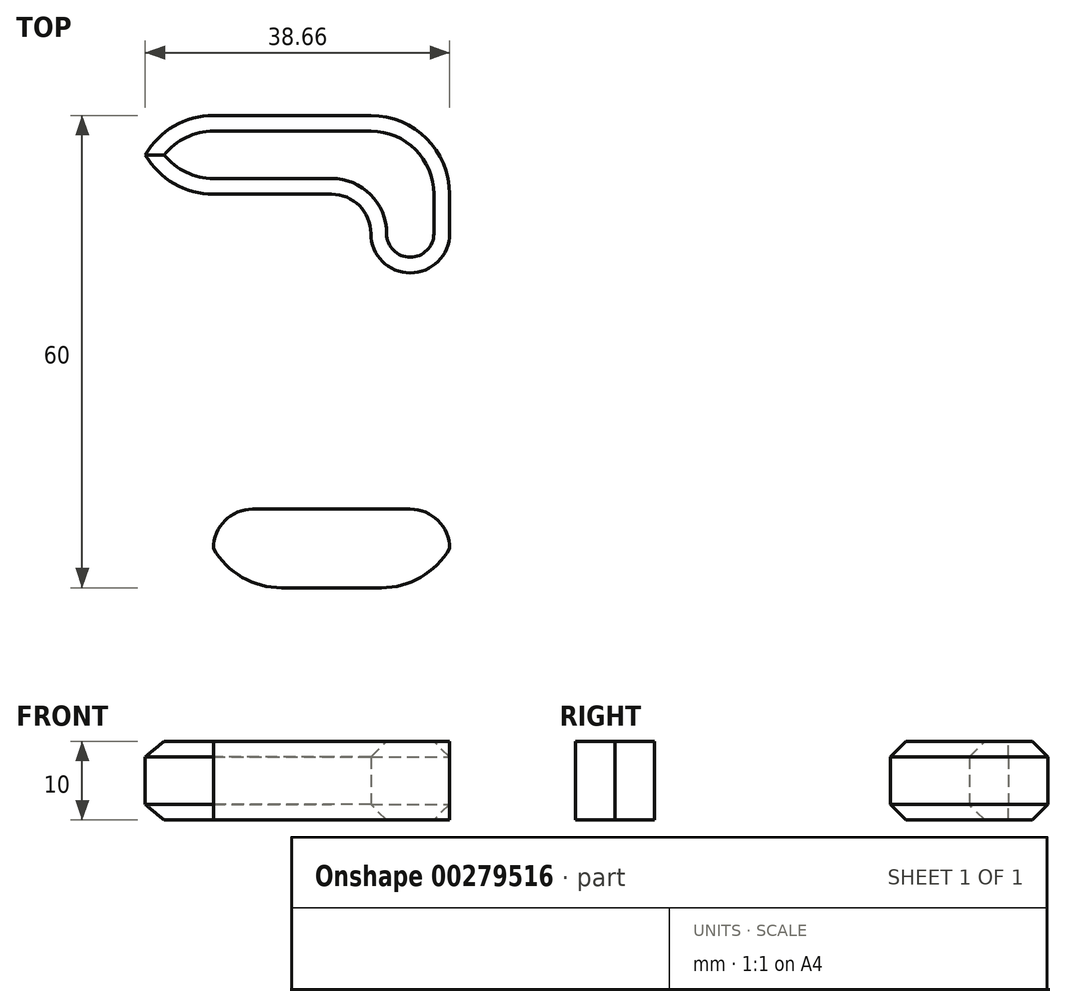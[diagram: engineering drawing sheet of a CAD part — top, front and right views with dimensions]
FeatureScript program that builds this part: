
annotation { "Feature Type Name" : "Feature", "Feature Type Description" : "" }
export const myFeature = defineFeature(function(context is Context, id is Id, definition is map)
    precondition{}
    {
        {
            var Q0;
            Q0=qCreatedBy(makeId("Top.planeOp"),FACE);
            var sketch = newSketch(context, id + "F0", { "sketchPlane" : qUnion([Q0])});
            skLineSegment(sketch, "E0.bottom", {"start": v(6.47, 40) * mm, "end": v(16.47, 40) * mm});
            skLineSegment(sketch, "E0.top", {"start": v(6.47, 20) * mm, "end": v(16.47, 20) * mm});
            skLineSegment(sketch, "E0.left", {"start": v(6.47, 40) * mm, "end": v(6.47, 20) * mm});
            skLineSegment(sketch, "E0.right", {"start": v(16.47, 40) * mm, "end": v(16.47, 20) * mm});
            skLineSegment(sketch, "E1.bottom", {"start": v(6.47, 40) * mm, "end": v(-23.53, 40) * mm});
            skLineSegment(sketch, "E1.top", {"start": v(6.47, 30) * mm, "end": v(-23.53, 30) * mm});
            skLineSegment(sketch, "E1.left", {"start": v(6.47, 40) * mm, "end": v(6.47, 30) * mm});
            skLineSegment(sketch, "E1.right", {"start": v(-23.53, 40) * mm, "end": v(-23.53, 30) * mm});
            skLineSegment(sketch, "E2.bottom", {"start": v(-23.53, 30) * mm, "end": v(-13.53, 30) * mm});
            skLineSegment(sketch, "E2.top", {"start": v(-23.53, -20) * mm, "end": v(-13.53, -20) * mm});
            skLineSegment(sketch, "E2.left", {"start": v(-23.53, 30) * mm, "end": v(-23.53, -20) * mm});
            skLineSegment(sketch, "E2.right", {"start": v(-13.53, 30) * mm, "end": v(-13.53, -20) * mm});
            skPoint(sketch, "E3.oppositeSnap0", {"position": v(-18.53, -20) * mm});
            skLineSegment(sketch, "E3.bottom", {"start": v(-13.53, -10) * mm, "end": v(16.47, -10) * mm});
            skLineSegment(sketch, "E3.top", {"start": v(-13.53, -20) * mm, "end": v(16.47, -20) * mm});
            skLineSegment(sketch, "E3.left", {"start": v(-13.53, -10) * mm, "end": v(-13.53, -20) * mm});
            skLineSegment(sketch, "E3.right", {"start": v(16.47, -10) * mm, "end": v(16.47, -20) * mm});
            skLineSegment(sketch, "E4.bottom", {"start": v(16.47, -10) * mm, "end": v(6.47, -10) * mm});
            skLineSegment(sketch, "E4.top", {"start": v(16.47, 0) * mm, "end": v(6.47, 0) * mm});
            skLineSegment(sketch, "E4.left", {"start": v(16.47, -10) * mm, "end": v(16.47, 0) * mm});
            skLineSegment(sketch, "E4.right", {"start": v(6.47, -10) * mm, "end": v(6.47, 0) * mm});
            skSolve(sketch);
        }
        {
            var Q0;
            Q0=makeQuery(id+"F0.imprint","IMPRINT",FACE,{"disambiguationData":[TD([[makeQuery(id+"F0.imprint","IMPRINT",EDGE,{"derivedFrom":sQuery(id+"F0.wireOp",EDGE,"E1.bottom")}),1.0]])]});
            var Q1;
            Q1=makeQuery(id+"F0.imprint","IMPRINT",FACE,{"disambiguationData":[TD([[makeQuery(id+"F0.imprint","IMPRINT",EDGE,{"derivedFrom":sQuery(id+"F0.wireOp",EDGE,"E0.bottom")}),-1.0]])]});
            var Q2;
            Q2=makeQuery(id+"F0.imprint","IMPRINT",FACE,{"disambiguationData":[TD([[makeQuery(id+"F0.imprint","IMPRINT",EDGE,{"derivedFrom":sQuery(id+"F0.wireOp",EDGE,"E2.bottom")}),-1.0]])]});
            var Q3;
            Q3=makeQuery(id+"F0.imprint","IMPRINT",FACE,{"disambiguationData":[TD([[makeQuery(id+"F0.imprint","IMPRINT",EDGE,{"derivedFrom":sQuery(id+"F0.wireOp",EDGE,"E3.bottom")}),-1.0]])]});
            var Q4;
            Q4=makeQuery(id+"F0.imprint","IMPRINT",FACE,{"disambiguationData":[TD([[makeQuery(id+"F0.imprint","IMPRINT",EDGE,{"derivedFrom":sQuery(id+"F0.wireOp",EDGE,"E4.bottom")}),-1.0]])]});
            extrude(context, id + "F1", {"entities" : qUnion([Q0, Q1, Q2, Q3, Q4]), "depth" : 10 * mm});
        }
        {
            var Q0;
            Q0=makeQuery(id+"F1.opExtrude","SWEPT_EDGE",EDGE,{"disambiguationData":[OSD([sQuery(id+"F0.wireOp",EDGE,"E4.top"),sQuery(id+"F0.wireOp",EDGE,"E4.left")])]});
            var Q1;
            Q1=makeQuery(id+"F1.opExtrude","SWEPT_EDGE",EDGE,{"disambiguationData":[OSD([sQuery(id+"F0.wireOp",EDGE,"E4.top"),sQuery(id+"F0.wireOp",EDGE,"E4.right")])]});
            var Q2;
            Q2=makeQuery(id+"F1.opExtrude","SWEPT_EDGE",EDGE,{"disambiguationData":[OSD([sQuery(id+"F0.wireOp",EDGE,"E2.right"),sQuery(id+"F0.wireOp",EDGE,"E3.bottom"),sQuery(id+"F0.wireOp",EDGE,"E3.left")])]});
            var Q3;
            Q3=makeQuery(id+"F1.opExtrude","SWEPT_EDGE",EDGE,{"disambiguationData":[OSD([sQuery(id+"F0.wireOp",EDGE,"E3.bottom"),sQuery(id+"F0.wireOp",EDGE,"E4.bottom"),sQuery(id+"F0.wireOp",EDGE,"E4.right")])]});
            var Q4;
            Q4=makeQuery(id+"F1.opExtrude","SWEPT_EDGE",EDGE,{"disambiguationData":[OSD([sQuery(id+"F0.wireOp",EDGE,"E0.top"),sQuery(id+"F0.wireOp",EDGE,"E0.left")])]});
            var Q5;
            Q5=makeQuery(id+"F1.opExtrude","SWEPT_EDGE",EDGE,{"disambiguationData":[OSD([sQuery(id+"F0.wireOp",EDGE,"E0.left"),sQuery(id+"F0.wireOp",EDGE,"E1.top"),sQuery(id+"F0.wireOp",EDGE,"E1.left")])]});
            var Q6;
            Q6=makeQuery(id+"F1.opExtrude","SWEPT_EDGE",EDGE,{"disambiguationData":[OSD([sQuery(id+"F0.wireOp",EDGE,"E1.top"),sQuery(id+"F0.wireOp",EDGE,"E2.bottom"),sQuery(id+"F0.wireOp",EDGE,"E2.right")])]});
            var Q7;
            Q7=makeQuery(id+"F1.opExtrude","SWEPT_EDGE",EDGE,{"disambiguationData":[OSD([sQuery(id+"F0.wireOp",EDGE,"E0.top"),sQuery(id+"F0.wireOp",EDGE,"E0.right")])]});
            fillet(context, id + "F2", {"entities" : qUnion([Q0, Q1, Q2, Q3, Q4, Q5, Q6, Q7]), "radius" : 5 * mm, "tangentPropagation" : true, "allowEdgeOverflow" : false});
        }
        {
            var Q0;
            Q0=makeQuery(id+"F1.opExtrude","SWEPT_EDGE",EDGE,{"disambiguationData":[OSD([sQuery(id+"F0.wireOp",EDGE,"E0.bottom"),sQuery(id+"F0.wireOp",EDGE,"E0.right")])]});
            var Q1;
            Q1=makeQuery(id+"F1.opExtrude","SWEPT_EDGE",EDGE,{"disambiguationData":[OSD([sQuery(id+"F0.wireOp",EDGE,"E1.bottom"),sQuery(id+"F0.wireOp",EDGE,"E1.right")])]});
            var Q2;
            Q2=makeQuery(id+"F1.opExtrude","SWEPT_EDGE",EDGE,{"disambiguationData":[OSD([sQuery(id+"F0.wireOp",EDGE,"E3.top"),sQuery(id+"F0.wireOp",EDGE,"E3.right")])]});
            var Q3;
            Q3=makeQuery(id+"F1.opExtrude","SWEPT_EDGE",EDGE,{"disambiguationData":[OSD([sQuery(id+"F0.wireOp",EDGE,"E2.top"),sQuery(id+"F0.wireOp",EDGE,"E2.left")])]});
            fillet(context, id + "F3", {"entities" : qUnion([Q0, Q1, Q2, Q3]), "radius" : 10 * mm, "tangentPropagation" : true, "allowEdgeOverflow" : false});
        }
        {
            var Q0;
            Q0=makeQuery(id+"F1.opExtrude","CAP_FACE",FACE,{"disambiguationData":[OSD([sQuery(id+"F0.wireOp",EDGE,"E0.bottom"),sQuery(id+"F0.wireOp",EDGE,"E0.top"),sQuery(id+"F0.wireOp",EDGE,"E0.left"),sQuery(id+"F0.wireOp",EDGE,"E0.right"),sQuery(id+"F0.wireOp",EDGE,"E1.bottom"),sQuery(id+"F0.wireOp",EDGE,"E1.top"),sQuery(id+"F0.wireOp",EDGE,"E1.right"),sQuery(id+"F0.wireOp",EDGE,"E2.top"),sQuery(id+"F0.wireOp",EDGE,"E2.left"),sQuery(id+"F0.wireOp",EDGE,"E2.right"),sQuery(id+"F0.wireOp",EDGE,"E3.bottom"),sQuery(id+"F0.wireOp",EDGE,"E3.top"),sQuery(id+"F0.wireOp",EDGE,"E3.right"),sQuery(id+"F0.wireOp",EDGE,"E4.top"),sQuery(id+"F0.wireOp",EDGE,"E4.left"),sQuery(id+"F0.wireOp",EDGE,"E4.right")])],"isStart":false});
            var Q1;
            Q1=makeQuery(id+"F1.opExtrude","CAP_FACE",FACE,{"disambiguationData":[OSD([sQuery(id+"F0.wireOp",EDGE,"E0.bottom"),sQuery(id+"F0.wireOp",EDGE,"E0.top"),sQuery(id+"F0.wireOp",EDGE,"E0.left"),sQuery(id+"F0.wireOp",EDGE,"E0.right"),sQuery(id+"F0.wireOp",EDGE,"E1.bottom"),sQuery(id+"F0.wireOp",EDGE,"E1.top"),sQuery(id+"F0.wireOp",EDGE,"E1.right"),sQuery(id+"F0.wireOp",EDGE,"E2.top"),sQuery(id+"F0.wireOp",EDGE,"E2.left"),sQuery(id+"F0.wireOp",EDGE,"E2.right"),sQuery(id+"F0.wireOp",EDGE,"E3.bottom"),sQuery(id+"F0.wireOp",EDGE,"E3.top"),sQuery(id+"F0.wireOp",EDGE,"E3.right"),sQuery(id+"F0.wireOp",EDGE,"E4.top"),sQuery(id+"F0.wireOp",EDGE,"E4.left"),sQuery(id+"F0.wireOp",EDGE,"E4.right")])],"isStart":true});
            chamfer(context, id + "F4", {"entities" : qUnion([Q0, Q1]), "width" : 2 * mm, "tangentPropagation" : true});
        }
    });
